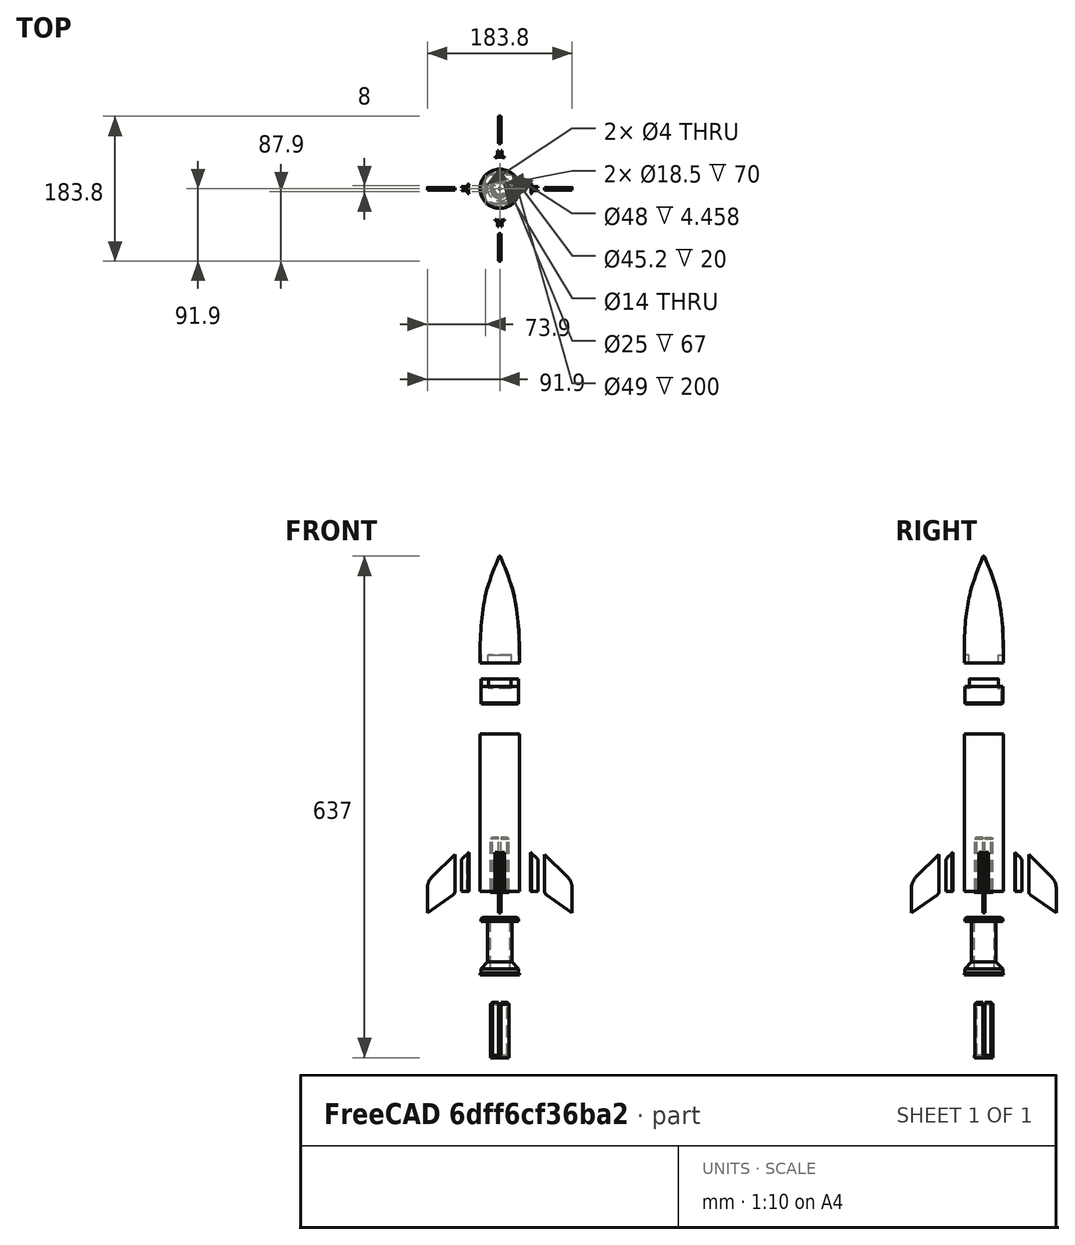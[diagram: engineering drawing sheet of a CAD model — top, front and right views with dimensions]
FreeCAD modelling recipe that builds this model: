
FCSTD DOCUMENT  (FreeCAD 0.19R)
Label: LaMule_V1_eclate
License: All rights reserved
LicenseURL: http://en.wikipedia.org/wiki/All_rights_reserved
objects: Sketcher::SketchObject×26, PartDesign::Pad×16, PartDesign::Body×14, PartDesign::Fillet×12, PartDesign::Pocket×8, PartDesign::Chamfer×7, Mesh::Feature×3, TechDraw::DrawViewSection×3, PartDesign::Revolution×2, App::LinkGroup×2, TechDraw::DrawViewDimension×2, PartDesign::Thickness×1, TechDraw::DrawSVGTemplate×1, TechDraw::DrawViewPart×1, TechDraw::DrawPage×1
note: 132 computed .brp shape members not serialized (recipe doc carries the construction recipe); baked Part::Feature solids carry a one-line shape summary decoded from their .brp

FEATURE [Sketcher::SketchObject] Sketch
  FullyConstrained = true
  MapMode = 5
  Placement = pos=(0,0,0) rot=(1,0,0;1.5708rad)
  Support = -> [XZ_Plane]
  sketch-geometry (12):
    g0: LineSegment StartX=24 StartY=0 StartZ=0 EndX=7 EndY=0 EndZ=0
    g1: LineSegment StartX=7 StartY=0 StartZ=0 EndX=7 EndY=3 EndZ=0
    g2: LineSegment StartX=7 StartY=3 StartZ=0 EndX=12.5 EndY=3 EndZ=0
    g3: LineSegment StartX=12.5 StartY=3 StartZ=0 EndX=12.5 EndY=73 EndZ=0
    g4: LineSegment StartX=12.5 StartY=73 StartZ=0 EndX=25 EndY=73 EndZ=0
    g5: LineSegment StartX=25 StartY=73 StartZ=0 EndX=25 EndY=71 EndZ=0
    g6: LineSegment StartX=25 StartY=71 StartZ=0 EndX=24 EndY=70 EndZ=0
    g7: LineSegment StartX=24 StartY=70 StartZ=0 EndX=24 EndY=65 EndZ=0
    g8: LineSegment StartX=24 StartY=65 StartZ=0 EndX=15.5 EndY=56.5 EndZ=0
    g9: LineSegment StartX=15.5 StartY=56.5 StartZ=0 EndX=15.5 EndY=5 EndZ=0
    g10: LineSegment StartX=15.5 StartY=5 StartZ=0 EndX=24 EndY=5 EndZ=0
    g11: LineSegment StartX=24 StartY=5 StartZ=0 EndX=24 EndY=0 EndZ=0
  constraints (36):
    c: PointOnObject(g0,g-1)
    c: PointOnObject(g0,g-1)
    c: Coincident(g0,g1)
    c: Vertical(g1)
    c: Coincident(g1,g2)
    c: Horizontal(g2)
    c: Coincident(g2,g3)
    c: Vertical(g3)
    c: Coincident(g3,g4)
    c: Horizontal(g4)
    c: Coincident(g4,g5)
    c: Coincident(g5,g6)
    c: Coincident(g6,g7)
    c: Vertical(g7)
    c: Coincident(g7,g8)
    c: Coincident(g8,g9)
    c: Vertical(g9)
    c: Coincident(g9,g10)
    c: Horizontal(g10)
    c: Coincident(g10,g11)
    c: Coincident(g11,g0)
    c: DistanceX(g-2,g2) = 12.5
    c: DistanceY(g3,g3) = 70
    c: DistanceY(g1,g1) = 3
    c: DistanceX(g-2,g4) = 25
    c: Vertical(g5)
    c: DistanceY(g5,g5) = 2
    c: DistanceY(g7,g7) = 5
    c: DistanceX(g-1,g0) = 24
    c: DistanceX(g-2,g7) = 24
    c: Distance(g9,g3) = 3
    c: DistanceY(g11,g11) = 5
    c: Angle(g9,g8) = 2.35619
    c: Angle(g7,g6) = 2.35619
    c: Vertical(g11)
    c: DistanceX(g-2,g0) = 7
FEATURE [PartDesign::Revolution] Revolution
  Angle = 360
  Axis = (0,2e-16,1)
  Base = (0,0,0)
  Placement = pos=(0,0,0) rot=(1,0,0;1.5708rad)
  Profile = -> Sketch
  ReferenceAxis = -> Sketch [V_Axis]
  Reversed = true
FEATURE [PartDesign::Chamfer] Chamfer
  Angle = 45
  Base = -> Revolution [Edge6]
  BaseFeature = -> Revolution
  ChamferType = 0
  FlipDirection = false
  Placement = pos=(0,0,0) rot=(1,0,0;1.5708rad)
  Size = 3
  Size2 = 1
  SupportTransform = false
FEATURE [PartDesign::Chamfer] Chamfer001
  Angle = 45
  Base = -> Chamfer [Edge12]
  BaseFeature = -> Chamfer
  ChamferType = 0
  FlipDirection = false
  Placement = pos=(0,0,0) rot=(1,0,0;1.5708rad)
  Size = 2
  Size2 = 1
  SupportTransform = false
FEATURE [PartDesign::Body] Body  label="support_moteur_V1"
  Group = -> [Sketch,Revolution,Chamfer,Chamfer001]
  Origin = -> Origin
  Placement = pos=(7e-15,0,-33) rot=(0,1,0;3.14159rad)
  Tip = -> Chamfer001
FEATURE [Sketcher::SketchObject] Sketch001
  FullyConstrained = true
  MapMode = 5
  Support = -> [XY_Plane001]
  sketch-geometry (2):
    g0: Circle CenterX=0 CenterY=0 CenterZ=0 NormalX=0 NormalY=0 NormalZ=1 AngleXU=0 Radius=24.5
    g1: Circle CenterX=0 CenterY=0 CenterZ=0 NormalX=0 NormalY=0 NormalZ=1 AngleXU=0 Radius=25
  constraints (4):
    c: Radius(g0) = 24.5
    c: Radius(g1) = 25
    c: Coincident(g0,g-1)
    c: Coincident(g1,g0)
FEATURE [PartDesign::Pad] Pad
  Direction = (1,1,1)
  Length = 200
  Length2 = 100
  Profile = -> Sketch001
  Type = 0
FEATURE [PartDesign::Body] Body001  label="tube_V1"
  Group = -> [Sketch001,Pad]
  Origin = -> Origin001
  Tip = -> Pad
FEATURE [Sketcher::SketchObject] Sketch002
  FullyConstrained = true
  MapMode = 5
  Support = -> [XY_Plane002]
  sketch-geometry (12):
    g0: ArcOfCircle CenterX=0 CenterY=0 CenterZ=0 NormalX=0 NormalY=0 NormalZ=1 AngleXU=0 Radius=25 StartAngle=6.04082 EndAngle=6.52555
    g1: LineSegment StartX=24.2693 StartY=-6 StartZ=0 EndX=25.2982 EndY=-6 EndZ=0
    g2: LineSegment StartX=24.2693 StartY=6 StartZ=0 EndX=25.2982 EndY=6 EndZ=0
    g3: LineSegment StartX=25.8697 StartY=2.6 StartZ=0 EndX=33.4517 EndY=2.6 EndZ=0
    g4: LineSegment StartX=33.4517 StartY=2.6 StartZ=0 EndX=33.4517 EndY=1.6 EndZ=0
    g5: LineSegment StartX=33.4517 StartY=1.6 StartZ=0 EndX=26.4517 EndY=1.6 EndZ=0
    g6: LineSegment StartX=26.4517 StartY=1.6 StartZ=0 EndX=26.4517 EndY=-1.6 EndZ=0
    g7: LineSegment StartX=26.4517 StartY=-1.6 StartZ=0 EndX=33.4517 EndY=-1.6 EndZ=0
    g8: LineSegment StartX=33.4517 StartY=-1.6 StartZ=0 EndX=33.4517 EndY=-2.6 EndZ=0
    g9: LineSegment StartX=33.4517 StartY=-2.6 StartZ=0 EndX=25.8697 EndY=-2.6 EndZ=0
    g10: ArcOfCircle CenterX=0 CenterY=0 CenterZ=0 NormalX=0 NormalY=0 NormalZ=1 AngleXU=0 Radius=26 StartAngle=6.05032 EndAngle=6.18302
    g11: ArcOfCircle CenterX=0 CenterY=0 CenterZ=0 NormalX=0 NormalY=0 NormalZ=1 AngleXU=0 Radius=26 StartAngle=0.100167 EndAngle=0.232868
  constraints (33):
    c: Coincident(g0,g-1)
    c: Radius(g0) = 25
    c: Coincident(g0,g1)
    c: Coincident(g0,g2)
    c: Horizontal(g3)
    c: Coincident(g3,g4)
    c: Coincident(g4,g5)
    c: Horizontal(g5)
    c: Coincident(g5,g6)
    c: Coincident(g6,g7)
    c: Horizontal(g7)
    c: Coincident(g7,g8)
    c: Coincident(g8,g9)
    c: Horizontal(g9)
    c: Coincident(g10,g0)
    c: Coincident(g10,g1)
    c: Coincident(g10,g9)
    c: Coincident(g11,g0)
    c: Coincident(g11,g2)
    c: Coincident(g11,g3)
    c: Radius(g11) = 26
    c: Horizontal(g2)
    c: Horizontal(g1)
    c: Symmetric(g7,g4,g-1)
    c: Vertical(g8)
    c: Vertical(g6)
    c: Distance(g6,g5) = 3.2
    c: DistanceY(g4,g4) = 1
    c: Distance(g5,g0) = 26.5
    c: Symmetric(g3,g8,g-1)
    c: DistanceX(g5,g5) = 7
    c: Symmetric(g2,g1,g-1)
    c: DistanceY(g-1,g2) = 6
FEATURE [PartDesign::Pad] Pad001
  Direction = (1,1,1)
  Length = 50
  Length2 = 100
  Profile = -> Sketch002
  Type = 0
FEATURE [PartDesign::Fillet] Fillet
  Base = -> Pad001 [Edge20,Edge1]
  BaseFeature = -> Pad001
  Radius = 4
  SupportTransform = false
FEATURE [Sketcher::SketchObject] Sketch003
  ExternalGeometry = -> [Fillet]
  FullyConstrained = true
  MapMode = 5
  Placement = pos=(0,-2.6,0) rot=(1,0,0;1.5708rad)
  Support = -> [Fillet]
  sketch-geometry (3):
    g0: LineSegment StartX=33.4517 StartY=50 StartZ=0 EndX=33.4517 EndY=40.8177 EndZ=0
    g1: LineSegment StartX=33.4517 StartY=40.8177 StartZ=0 EndX=24.2693 EndY=50 EndZ=0
    g2: LineSegment StartX=24.2693 StartY=50 StartZ=0 EndX=33.4517 EndY=50 EndZ=0
  constraints (8):
    c: Coincident(g-4,g0)
    c: PointOnObject(g0,g-4)
    c: Coincident(g0,g1)
    c: PointOnObject(g1,g-3)
    c: Coincident(g1,g2)
    c: Coincident(g2,g0)
    c: Horizontal(g2)
    c: Angle(g1,g2) = 0.785398
FEATURE [PartDesign::Pocket] Pocket
  BaseFeature = -> Fillet
  Length = 23
  Length2 = 100
  Midplane = true
  Profile = -> Sketch003
  Type = 1
FEATURE [PartDesign::Body] Body002  label="support_aileron_V1"
  Group = -> [Sketch002,Pad001,Fillet,Sketch003,Pocket]
  Origin = -> Origin002
  Placement = pos=(15,0,0) rot=(0,0,1;0rad)
  Tip = -> Pocket
FEATURE [Sketcher::SketchObject] Sketch004
  FullyConstrained = true
  MapMode = 5
  Support = -> [XY_Plane003]
  sketch-geometry (12):
    g0: ArcOfCircle CenterX=0 CenterY=0 CenterZ=0 NormalX=0 NormalY=0 NormalZ=1 AngleXU=0 Radius=25 StartAngle=6.04082 EndAngle=6.52555
    g1: LineSegment StartX=24.2693 StartY=-6 StartZ=0 EndX=25.2982 EndY=-6 EndZ=0
    g2: LineSegment StartX=24.2693 StartY=6 StartZ=0 EndX=25.2982 EndY=6 EndZ=0
    g3: LineSegment StartX=25.8697 StartY=2.6 StartZ=0 EndX=33.4517 EndY=2.6 EndZ=0
    g4: LineSegment StartX=33.4517 StartY=2.6 StartZ=0 EndX=33.4517 EndY=1.6 EndZ=0
    g5: LineSegment StartX=33.4517 StartY=1.6 StartZ=0 EndX=26.4517 EndY=1.6 EndZ=0
    g6: LineSegment StartX=26.4517 StartY=1.6 StartZ=0 EndX=26.4517 EndY=-1.6 EndZ=0
    g7: LineSegment StartX=26.4517 StartY=-1.6 StartZ=0 EndX=33.4517 EndY=-1.6 EndZ=0
    g8: LineSegment StartX=33.4517 StartY=-1.6 StartZ=0 EndX=33.4517 EndY=-2.6 EndZ=0
    g9: LineSegment StartX=33.4517 StartY=-2.6 StartZ=0 EndX=25.8697 EndY=-2.6 EndZ=0
    g10: ArcOfCircle CenterX=0 CenterY=0 CenterZ=0 NormalX=0 NormalY=0 NormalZ=1 AngleXU=0 Radius=26 StartAngle=6.05032 EndAngle=6.18302
    g11: ArcOfCircle CenterX=0 CenterY=0 CenterZ=0 NormalX=0 NormalY=0 NormalZ=1 AngleXU=0 Radius=26 StartAngle=0.100167 EndAngle=0.232868
  constraints (33):
    c: Coincident(g0,g-1)
    c: Radius(g0) = 25
    c: Coincident(g0,g1)
    c: Coincident(g0,g2)
    c: Horizontal(g3)
    c: Coincident(g3,g4)
    c: Coincident(g4,g5)
    c: Horizontal(g5)
    c: Coincident(g5,g6)
    c: Coincident(g6,g7)
    c: Horizontal(g7)
    c: Coincident(g7,g8)
    c: Coincident(g8,g9)
    c: Horizontal(g9)
    c: Coincident(g10,g0)
    c: Coincident(g10,g1)
    c: Coincident(g10,g9)
    c: Coincident(g11,g0)
    c: Coincident(g11,g2)
    c: Coincident(g11,g3)
    c: Radius(g11) = 26
    c: Horizontal(g2)
    c: Horizontal(g1)
    c: Symmetric(g7,g4,g-1)
    c: Vertical(g8)
    c: Vertical(g6)
    c: Distance(g6,g5) = 3.2
    c: DistanceY(g4,g4) = 1
    c: Distance(g5,g0) = 26.5
    c: Symmetric(g3,g8,g-1)
    c: DistanceX(g5,g5) = 7
    c: Symmetric(g2,g1,g-1)
    c: DistanceY(g-1,g2) = 6
FEATURE [PartDesign::Pad] Pad002
  Direction = (1,1,1)
  Length = 50
  Length2 = 100
  Profile = -> Sketch004
  Type = 0
FEATURE [PartDesign::Fillet] Fillet001
  Base = -> Pad002 [Edge20,Edge1]
  BaseFeature = -> Pad002
  Radius = 4
  SupportTransform = false
FEATURE [Sketcher::SketchObject] Sketch005
  ExternalGeometry = -> [Fillet001]
  FullyConstrained = true
  MapMode = 5
  Placement = pos=(0,-2.6,0) rot=(1,0,0;1.5708rad)
  Support = -> [Fillet001]
  sketch-geometry (3):
    g0: LineSegment StartX=33.4517 StartY=50 StartZ=0 EndX=33.4517 EndY=40.8177 EndZ=0
    g1: LineSegment StartX=33.4517 StartY=40.8177 StartZ=0 EndX=24.2693 EndY=50 EndZ=0
    g2: LineSegment StartX=24.2693 StartY=50 StartZ=0 EndX=33.4517 EndY=50 EndZ=0
  constraints (8):
    c: Coincident(g-4,g0)
    c: PointOnObject(g0,g-4)
    c: Coincident(g0,g1)
    c: PointOnObject(g1,g-3)
    c: Coincident(g1,g2)
    c: Coincident(g2,g0)
    c: Horizontal(g2)
    c: Angle(g1,g2) = 0.785398
FEATURE [PartDesign::Pocket] Pocket001
  BaseFeature = -> Fillet001
  Length = 23
  Length2 = 100
  Midplane = true
  Profile = -> Sketch005
  Type = 1
FEATURE [PartDesign::Body] Body003  label="support_aileron_V002"
  Group = -> [Sketch004,Pad002,Fillet001,Sketch005,Pocket001]
  Origin = -> Origin003
  Placement = pos=(3.3e-15,15,0) rot=(0,0,1;1.5708rad)
  Tip = -> Pocket001
FEATURE [Sketcher::SketchObject] Sketch006
  FullyConstrained = true
  MapMode = 5
  Support = -> [XY_Plane004]
  sketch-geometry (12):
    g0: ArcOfCircle CenterX=0 CenterY=0 CenterZ=0 NormalX=0 NormalY=0 NormalZ=1 AngleXU=0 Radius=25 StartAngle=6.04082 EndAngle=6.52555
    g1: LineSegment StartX=24.2693 StartY=-6 StartZ=0 EndX=25.2982 EndY=-6 EndZ=0
    g2: LineSegment StartX=24.2693 StartY=6 StartZ=0 EndX=25.2982 EndY=6 EndZ=0
    g3: LineSegment StartX=25.8697 StartY=2.6 StartZ=0 EndX=33.4517 EndY=2.6 EndZ=0
    g4: LineSegment StartX=33.4517 StartY=2.6 StartZ=0 EndX=33.4517 EndY=1.6 EndZ=0
    g5: LineSegment StartX=33.4517 StartY=1.6 StartZ=0 EndX=26.4517 EndY=1.6 EndZ=0
    g6: LineSegment StartX=26.4517 StartY=1.6 StartZ=0 EndX=26.4517 EndY=-1.6 EndZ=0
    g7: LineSegment StartX=26.4517 StartY=-1.6 StartZ=0 EndX=33.4517 EndY=-1.6 EndZ=0
    g8: LineSegment StartX=33.4517 StartY=-1.6 StartZ=0 EndX=33.4517 EndY=-2.6 EndZ=0
    g9: LineSegment StartX=33.4517 StartY=-2.6 StartZ=0 EndX=25.8697 EndY=-2.6 EndZ=0
    g10: ArcOfCircle CenterX=0 CenterY=0 CenterZ=0 NormalX=0 NormalY=0 NormalZ=1 AngleXU=0 Radius=26 StartAngle=6.05032 EndAngle=6.18302
    g11: ArcOfCircle CenterX=0 CenterY=0 CenterZ=0 NormalX=0 NormalY=0 NormalZ=1 AngleXU=0 Radius=26 StartAngle=0.100167 EndAngle=0.232868
  constraints (33):
    c: Coincident(g0,g-1)
    c: Radius(g0) = 25
    c: Coincident(g0,g1)
    c: Coincident(g0,g2)
    c: Horizontal(g3)
    c: Coincident(g3,g4)
    c: Coincident(g4,g5)
    c: Horizontal(g5)
    c: Coincident(g5,g6)
    c: Coincident(g6,g7)
    c: Horizontal(g7)
    c: Coincident(g7,g8)
    c: Coincident(g8,g9)
    c: Horizontal(g9)
    c: Coincident(g10,g0)
    c: Coincident(g10,g1)
    c: Coincident(g10,g9)
    c: Coincident(g11,g0)
    c: Coincident(g11,g2)
    c: Coincident(g11,g3)
    c: Radius(g11) = 26
    c: Horizontal(g2)
    c: Horizontal(g1)
    c: Symmetric(g7,g4,g-1)
    c: Vertical(g8)
    c: Vertical(g6)
    c: Distance(g6,g5) = 3.2
    c: DistanceY(g4,g4) = 1
    c: Distance(g5,g0) = 26.5
    c: Symmetric(g3,g8,g-1)
    c: DistanceX(g5,g5) = 7
    c: Symmetric(g2,g1,g-1)
    c: DistanceY(g-1,g2) = 6
FEATURE [PartDesign::Pad] Pad003
  Direction = (1,1,1)
  Length = 50
  Length2 = 100
  Profile = -> Sketch006
  Type = 0
FEATURE [PartDesign::Fillet] Fillet002
  Base = -> Pad003 [Edge20,Edge1]
  BaseFeature = -> Pad003
  Radius = 4
  SupportTransform = false
FEATURE [Sketcher::SketchObject] Sketch007
  ExternalGeometry = -> [Fillet002]
  FullyConstrained = true
  MapMode = 5
  Placement = pos=(0,-2.6,0) rot=(1,0,0;1.5708rad)
  Support = -> [Fillet002]
  sketch-geometry (3):
    g0: LineSegment StartX=33.4517 StartY=50 StartZ=0 EndX=33.4517 EndY=40.8177 EndZ=0
    g1: LineSegment StartX=33.4517 StartY=40.8177 StartZ=0 EndX=24.2693 EndY=50 EndZ=0
    g2: LineSegment StartX=24.2693 StartY=50 StartZ=0 EndX=33.4517 EndY=50 EndZ=0
  constraints (8):
    c: Coincident(g-4,g0)
    c: PointOnObject(g0,g-4)
    c: Coincident(g0,g1)
    c: PointOnObject(g1,g-3)
    c: Coincident(g1,g2)
    c: Coincident(g2,g0)
    c: Horizontal(g2)
    c: Angle(g1,g2) = 0.785398
FEATURE [PartDesign::Pocket] Pocket002
  BaseFeature = -> Fillet002
  Length = 23
  Length2 = 100
  Midplane = true
  Profile = -> Sketch007
  Type = 1
FEATURE [PartDesign::Body] Body004  label="support_aileron_V003"
  Group = -> [Sketch006,Pad003,Fillet002,Sketch007,Pocket002]
  Origin = -> Origin004
  Placement = pos=(-15,0,0) rot=(0,0,1;3.14159rad)
  Tip = -> Pocket002
FEATURE [Sketcher::SketchObject] Sketch008
  FullyConstrained = true
  MapMode = 5
  Support = -> [XY_Plane005]
  sketch-geometry (12):
    g0: ArcOfCircle CenterX=0 CenterY=0 CenterZ=0 NormalX=0 NormalY=0 NormalZ=1 AngleXU=0 Radius=25 StartAngle=6.04082 EndAngle=6.52555
    g1: LineSegment StartX=24.2693 StartY=-6 StartZ=0 EndX=25.2982 EndY=-6 EndZ=0
    g2: LineSegment StartX=24.2693 StartY=6 StartZ=0 EndX=25.2982 EndY=6 EndZ=0
    g3: LineSegment StartX=25.8697 StartY=2.6 StartZ=0 EndX=33.4517 EndY=2.6 EndZ=0
    g4: LineSegment StartX=33.4517 StartY=2.6 StartZ=0 EndX=33.4517 EndY=1.6 EndZ=0
    g5: LineSegment StartX=33.4517 StartY=1.6 StartZ=0 EndX=26.4517 EndY=1.6 EndZ=0
    g6: LineSegment StartX=26.4517 StartY=1.6 StartZ=0 EndX=26.4517 EndY=-1.6 EndZ=0
    g7: LineSegment StartX=26.4517 StartY=-1.6 StartZ=0 EndX=33.4517 EndY=-1.6 EndZ=0
    g8: LineSegment StartX=33.4517 StartY=-1.6 StartZ=0 EndX=33.4517 EndY=-2.6 EndZ=0
    g9: LineSegment StartX=33.4517 StartY=-2.6 StartZ=0 EndX=25.8697 EndY=-2.6 EndZ=0
    g10: ArcOfCircle CenterX=0 CenterY=0 CenterZ=0 NormalX=0 NormalY=0 NormalZ=1 AngleXU=0 Radius=26 StartAngle=6.05032 EndAngle=6.18302
    g11: ArcOfCircle CenterX=0 CenterY=0 CenterZ=0 NormalX=0 NormalY=0 NormalZ=1 AngleXU=0 Radius=26 StartAngle=0.100167 EndAngle=0.232868
  constraints (33):
    c: Coincident(g0,g-1)
    c: Radius(g0) = 25
    c: Coincident(g0,g1)
    c: Coincident(g0,g2)
    c: Horizontal(g3)
    c: Coincident(g3,g4)
    c: Coincident(g4,g5)
    c: Horizontal(g5)
    c: Coincident(g5,g6)
    c: Coincident(g6,g7)
    c: Horizontal(g7)
    c: Coincident(g7,g8)
    c: Coincident(g8,g9)
    c: Horizontal(g9)
    c: Coincident(g10,g0)
    c: Coincident(g10,g1)
    c: Coincident(g10,g9)
    c: Coincident(g11,g0)
    c: Coincident(g11,g2)
    c: Coincident(g11,g3)
    c: Radius(g11) = 26
    c: Horizontal(g2)
    c: Horizontal(g1)
    c: Symmetric(g7,g4,g-1)
    c: Vertical(g8)
    c: Vertical(g6)
    c: Distance(g6,g5) = 3.2
    c: DistanceY(g4,g4) = 1
    c: Distance(g5,g0) = 26.5
    c: Symmetric(g3,g8,g-1)
    c: DistanceX(g5,g5) = 7
    c: Symmetric(g2,g1,g-1)
    c: DistanceY(g-1,g2) = 6
FEATURE [PartDesign::Pad] Pad004
  Direction = (1,1,1)
  Length = 50
  Length2 = 100
  Profile = -> Sketch008
  Type = 0
FEATURE [PartDesign::Fillet] Fillet003
  Base = -> Pad004 [Edge20,Edge1]
  BaseFeature = -> Pad004
  Radius = 4
  SupportTransform = false
FEATURE [Sketcher::SketchObject] Sketch009
  ExternalGeometry = -> [Fillet003]
  FullyConstrained = true
  MapMode = 5
  Placement = pos=(0,-2.6,0) rot=(1,0,0;1.5708rad)
  Support = -> [Fillet003]
  sketch-geometry (3):
    g0: LineSegment StartX=33.4517 StartY=50 StartZ=0 EndX=33.4517 EndY=40.8177 EndZ=0
    g1: LineSegment StartX=33.4517 StartY=40.8177 StartZ=0 EndX=24.2693 EndY=50 EndZ=0
    g2: LineSegment StartX=24.2693 StartY=50 StartZ=0 EndX=33.4517 EndY=50 EndZ=0
  constraints (8):
    c: Coincident(g-4,g0)
    c: PointOnObject(g0,g-4)
    c: Coincident(g0,g1)
    c: PointOnObject(g1,g-3)
    c: Coincident(g1,g2)
    c: Coincident(g2,g0)
    c: Horizontal(g2)
    c: Angle(g1,g2) = 0.785398
FEATURE [PartDesign::Pocket] Pocket003
  BaseFeature = -> Fillet003
  Length = 23
  Length2 = 100
  Midplane = true
  Profile = -> Sketch009
  Type = 1
FEATURE [PartDesign::Body] Body005  label="support_aileron_V004"
  Group = -> [Sketch008,Pad004,Fillet003,Sketch009,Pocket003]
  Origin = -> Origin005
  Placement = pos=(3.3e-15,-15,0) rot=(0,0,-1;1.5708rad)
  Tip = -> Pocket003
FEATURE [App::LinkGroup] LinkGroup  label="support_ailerons_V1"
  ElementList = -> [Body005,Body004,Body003,Body002]
  LinkMode = 0
FEATURE [Sketcher::SketchObject] Sketch010
  FullyConstrained = true
  MapMode = 5
  Placement = pos=(0,0,0) rot=(0.57735,0.57735,0.57735;2.0944rad)
  Support = -> [YZ_Plane006]
  sketch-geometry (4):
    g0: LineSegment StartX=27 StartY=-2.5 StartZ=0 EndX=61.9 EndY=-27.4 EndZ=0
    g1: LineSegment StartX=61.9 StartY=-27.4 StartZ=0 EndX=61.9 EndY=12.6 EndZ=0
    g2: LineSegment StartX=61.9 StartY=12.6 StartZ=0 EndX=27 EndY=47.5 EndZ=0
    g3: LineSegment StartX=27 StartY=47.5 StartZ=0 EndX=27 EndY=-2.5 EndZ=0
  constraints (12):
    c: Coincident(g0,g1)
    c: Vertical(g1)
    c: Coincident(g1,g2)
    c: Coincident(g2,g3)
    c: Coincident(g3,g0)
    c: Vertical(g3)
    c: DistanceY(g3,g3) = 50
    c: DistanceY(g-1,g2) = 47.5
    c: DistanceX(g-2,g0) = 27
    c: Angle(g3,g2) = 0.785398
    c: DistanceY(g1,g1) = 40
    c: DistanceX(g-2,g0) = 61.9
FEATURE [PartDesign::Pad] Pad005
  Direction = (1,1,1)
  Length = 3
  Length2 = 100
  Midplane = true
  Placement = pos=(0,0,0) rot=(0.57735,0.57735,0.57735;2.0944rad)
  Profile = -> Sketch010
  Type = 0
FEATURE [PartDesign::Fillet] Fillet004
  Base = -> Pad005 [Edge5]
  BaseFeature = -> Pad005
  Placement = pos=(0,0,0) rot=(0.57735,0.57735,0.57735;2.0944rad)
  Radius = 20
  SupportTransform = false
FEATURE [PartDesign::Fillet] Fillet005
  Base = -> Fillet004 [Edge11]
  BaseFeature = -> Fillet004
  Placement = pos=(0,0,0) rot=(0.57735,0.57735,0.57735;2.0944rad)
  Radius = 5
  SupportTransform = false
FEATURE [PartDesign::Body] Body006  label="ailerons_V1"
  Group = -> [Sketch010,Pad005,Fillet004,Fillet005]
  Origin = -> Origin006
  Placement = pos=(0,30,0) rot=(0,0,1;0rad)
  Tip = -> Fillet005
FEATURE [Sketcher::SketchObject] Sketch011
  FullyConstrained = true
  MapMode = 5
  Placement = pos=(0,0,0) rot=(0.57735,0.57735,0.57735;2.0944rad)
  Support = -> [YZ_Plane007]
  sketch-geometry (4):
    g0: LineSegment StartX=27 StartY=-2.5 StartZ=0 EndX=61.9 EndY=-27.4 EndZ=0
    g1: LineSegment StartX=61.9 StartY=-27.4 StartZ=0 EndX=61.9 EndY=12.6 EndZ=0
    g2: LineSegment StartX=61.9 StartY=12.6 StartZ=0 EndX=27 EndY=47.5 EndZ=0
    g3: LineSegment StartX=27 StartY=47.5 StartZ=0 EndX=27 EndY=-2.5 EndZ=0
  constraints (12):
    c: Coincident(g0,g1)
    c: Vertical(g1)
    c: Coincident(g1,g2)
    c: Coincident(g2,g3)
    c: Coincident(g3,g0)
    c: Vertical(g3)
    c: DistanceY(g3,g3) = 50
    c: DistanceY(g-1,g2) = 47.5
    c: DistanceX(g-2,g0) = 27
    c: Angle(g3,g2) = 0.785398
    c: DistanceY(g1,g1) = 40
    c: DistanceX(g-2,g0) = 61.9
FEATURE [PartDesign::Pad] Pad006
  Direction = (1,1,1)
  Length = 3
  Length2 = 100
  Midplane = true
  Placement = pos=(0,0,0) rot=(0.57735,0.57735,0.57735;2.0944rad)
  Profile = -> Sketch011
  Type = 0
FEATURE [PartDesign::Fillet] Fillet006
  Base = -> Pad006 [Edge5]
  BaseFeature = -> Pad006
  Placement = pos=(0,0,0) rot=(0.57735,0.57735,0.57735;2.0944rad)
  Radius = 20
  SupportTransform = false
FEATURE [PartDesign::Fillet] Fillet007
  Base = -> Fillet006 [Edge11]
  BaseFeature = -> Fillet006
  Placement = pos=(0,0,0) rot=(0.57735,0.57735,0.57735;2.0944rad)
  Radius = 5
  SupportTransform = false
FEATURE [PartDesign::Body] Body007  label="ailerons_V002"
  Group = -> [Sketch011,Pad006,Fillet006,Fillet007]
  Origin = -> Origin007
  Placement = pos=(0,-30,0) rot=(0,0,1;3.14159rad)
  Tip = -> Fillet007
FEATURE [Sketcher::SketchObject] Sketch012
  FullyConstrained = true
  MapMode = 5
  Placement = pos=(0,0,0) rot=(0.57735,0.57735,0.57735;2.0944rad)
  Support = -> [YZ_Plane008]
  sketch-geometry (4):
    g0: LineSegment StartX=27 StartY=-2.5 StartZ=0 EndX=61.9 EndY=-27.4 EndZ=0
    g1: LineSegment StartX=61.9 StartY=-27.4 StartZ=0 EndX=61.9 EndY=12.6 EndZ=0
    g2: LineSegment StartX=61.9 StartY=12.6 StartZ=0 EndX=27 EndY=47.5 EndZ=0
    g3: LineSegment StartX=27 StartY=47.5 StartZ=0 EndX=27 EndY=-2.5 EndZ=0
  constraints (12):
    c: Coincident(g0,g1)
    c: Vertical(g1)
    c: Coincident(g1,g2)
    c: Coincident(g2,g3)
    c: Coincident(g3,g0)
    c: Vertical(g3)
    c: DistanceY(g3,g3) = 50
    c: DistanceY(g-1,g2) = 47.5
    c: DistanceX(g-2,g0) = 27
    c: Angle(g3,g2) = 0.785398
    c: DistanceY(g1,g1) = 40
    c: DistanceX(g-2,g0) = 61.9
FEATURE [PartDesign::Pad] Pad007
  Direction = (1,1,1)
  Length = 3
  Length2 = 100
  Midplane = true
  Placement = pos=(0,0,0) rot=(0.57735,0.57735,0.57735;2.0944rad)
  Profile = -> Sketch012
  Type = 0
FEATURE [PartDesign::Fillet] Fillet008
  Base = -> Pad007 [Edge5]
  BaseFeature = -> Pad007
  Placement = pos=(0,0,0) rot=(0.57735,0.57735,0.57735;2.0944rad)
  Radius = 20
  SupportTransform = false
FEATURE [PartDesign::Fillet] Fillet009
  Base = -> Fillet008 [Edge11]
  BaseFeature = -> Fillet008
  Placement = pos=(0,0,0) rot=(0.57735,0.57735,0.57735;2.0944rad)
  Radius = 5
  SupportTransform = false
FEATURE [PartDesign::Body] Body008  label="ailerons_V003"
  Group = -> [Sketch012,Pad007,Fillet008,Fillet009]
  Origin = -> Origin008
  Placement = pos=(-30,6.7e-15,0) rot=(0,0,1;1.5708rad)
  Tip = -> Fillet009
FEATURE [Sketcher::SketchObject] Sketch013
  FullyConstrained = true
  MapMode = 5
  Placement = pos=(0,0,0) rot=(0.57735,0.57735,0.57735;2.0944rad)
  Support = -> [YZ_Plane009]
  sketch-geometry (4):
    g0: LineSegment StartX=27 StartY=-2.5 StartZ=0 EndX=61.9 EndY=-27.4 EndZ=0
    g1: LineSegment StartX=61.9 StartY=-27.4 StartZ=0 EndX=61.9 EndY=12.6 EndZ=0
    g2: LineSegment StartX=61.9 StartY=12.6 StartZ=0 EndX=27 EndY=47.5 EndZ=0
    g3: LineSegment StartX=27 StartY=47.5 StartZ=0 EndX=27 EndY=-2.5 EndZ=0
  constraints (12):
    c: Coincident(g0,g1)
    c: Vertical(g1)
    c: Coincident(g1,g2)
    c: Coincident(g2,g3)
    c: Coincident(g3,g0)
    c: Vertical(g3)
    c: DistanceY(g3,g3) = 50
    c: DistanceY(g-1,g2) = 47.5
    c: DistanceX(g-2,g0) = 27
    c: Angle(g3,g2) = 0.785398
    c: DistanceY(g1,g1) = 40
    c: DistanceX(g-2,g0) = 61.9
FEATURE [PartDesign::Pad] Pad008
  Direction = (1,1,1)
  Length = 3
  Length2 = 100
  Midplane = true
  Placement = pos=(0,0,0) rot=(0.57735,0.57735,0.57735;2.0944rad)
  Profile = -> Sketch013
  Type = 0
FEATURE [PartDesign::Fillet] Fillet010
  Base = -> Pad008 [Edge5]
  BaseFeature = -> Pad008
  Placement = pos=(0,0,0) rot=(0.57735,0.57735,0.57735;2.0944rad)
  Radius = 20
  SupportTransform = false
FEATURE [PartDesign::Fillet] Fillet011
  Base = -> Fillet010 [Edge11]
  BaseFeature = -> Fillet010
  Placement = pos=(0,0,0) rot=(0.57735,0.57735,0.57735;2.0944rad)
  Radius = 5
  SupportTransform = false
FEATURE [PartDesign::Body] Body009  label="ailerons_V004"
  Group = -> [Sketch013,Pad008,Fillet010,Fillet011]
  Origin = -> Origin009
  Placement = pos=(30,6.7e-15,0) rot=(0,0,-1;1.5708rad)
  Tip = -> Fillet011
FEATURE [App::LinkGroup] LinkGroup001  label="ailerons"
  ElementList = -> [Body009,Body008,Body007,Body006]
  LinkMode = 0
FEATURE [Sketcher::SketchObject] Sketch014
  FullyConstrained = true
  MapMode = 5
  Support = -> [XY_Plane010]
  sketch-geometry (12):
    g0: LineSegment StartX=0 StartY=0 StartZ=0 EndX=134.73 EndY=0 EndZ=0
    g1: LineSegment StartX=134.73 StartY=-24 StartZ=0 EndX=134.73 EndY=0 EndZ=0
    g2: LineSegment StartX=134.73 StartY=-24 StartZ=0 EndX=120.272 EndY=-24 EndZ=0
    g3-g7: Circle x5 (B-spline internal-alignment scaffolding for g8; pole/knot coordinates omitted)
    g8: BSplineCurve PolesCount=5 KnotsCount=3 Degree=3 IsPeriodic=0
    g9: GeomPoint X=120.272 Y=-24 Z=0
    g10: GeomPoint X=62.1183 Y=-19.6849 Z=0
    g11: GeomPoint X=0 Y=0 Z=0
  constraints (23):
    c: Coincident(g0,g-1)
    c: PointOnObject(g0,g-1)
    c: Coincident(g1,g0)
    c: Vertical(g1)
    c: Coincident(g2,g1)
    c: Horizontal(g2)
    c: Coincident(g8,g2)
    c: Weight(g3) = 1
    c: Equal(g3, g4-g7) x4
    c: Coincident(g8,g0)
    c: InternalAlignment(g3-g7 -> g8) x5
    c: InternalAlignment(g9,g8)
    c: InternalAlignment(g10,g8)
    c: InternalAlignment(g11,g8)
    c: DistanceX(g6) = 33.4091
    c: DistanceY(g6) = -14.1378
    c: DistanceX(g5) = 61.0359
    c: DistanceY(g5) = -20.426
    c: DistanceX(g4) = 92.9923
    c: DistanceY(g4) = -23.75
    c: DistanceX(g2) = 120.272
    c: DistanceY(g2) = -24
    c: DistanceX(g0,g0) = 134.73
FEATURE [PartDesign::Revolution] Revolution001
  Angle = 360
  Axis = (1,0,0)
  Base = (0,0,0)
  Profile = -> Sketch014
  ReferenceAxis = -> X_Axis010
  Reversed = true
FEATURE [PartDesign::Thickness] Thickness
  Base = -> Revolution001 [Face1]
  BaseFeature = -> Revolution001
  Intersection = false
  Join = 0
  Mode = 0
  SupportTransform = false
  Value = 1
FEATURE [Sketcher::SketchObject] Sketch015
  FullyConstrained = true
  MapMode = 5
  Placement = pos=(134.73,0,0) rot=(0.57735,0.57735,0.57735;2.0944rad)
  Support = -> [Thickness]
  sketch-geometry (5):
    g0: Circle CenterX=1.1e-15 CenterY=0 CenterZ=0 NormalX=0 NormalY=0 NormalZ=1 AngleXU=0 Radius=25
    g1: ArcOfCircle CenterX=1.1e-15 CenterY=0 CenterZ=0 NormalX=0 NormalY=0 NormalZ=1 AngleXU=0 Radius=24 StartAngle=0.675132 EndAngle=2.46646
    g2: ArcOfCircle CenterX=1.1e-15 CenterY=0 CenterZ=0 NormalX=0 NormalY=0 NormalZ=1 AngleXU=0 Radius=24 StartAngle=3.81672 EndAngle=5.60805
    g3: LineSegment StartX=-18.735 StartY=15 StartZ=0 EndX=-18.735 EndY=-15 EndZ=0
    g4: LineSegment StartX=18.735 StartY=15 StartZ=0 EndX=18.735 EndY=-15 EndZ=0
  constraints (14):
    c: Coincident(g0,g-1)
    c: Radius(g0) = 25
    c: Coincident(g1,g0)
    c: Coincident(g2,g0)
    c: Symmetric(g2,g2,g-2)
    c: Symmetric(g2,g1,g-1)
    c: Radius(g1) = 24
    c: Equal(g1,g2)
    c: Coincident(g3,g1)
    c: Coincident(g3,g2)
    c: Coincident(g4,g1)
    c: Coincident(g4,g2)
    c: Symmetric(g1,g1,g-2)
    c: DistanceY(g4,g4) = 30
FEATURE [PartDesign::Pad] Pad009
  BaseFeature = -> Thickness
  Direction = (1,1,1)
  Length = 10
  Length2 = 100
  Profile = -> Sketch015
  Reversed = true
  Type = 0
FEATURE [PartDesign::Chamfer] Chamfer002
  Angle = 45
  Base = -> Pad009 [Edge9,Edge6]
  BaseFeature = -> Pad009
  ChamferType = 0
  FlipDirection = false
  Size = 1
  Size2 = 1
  SupportTransform = false
FEATURE [PartDesign::Body] Body010  label="coiffe_V1"
  Group = -> [Sketch014,Revolution001,Thickness,Sketch015,Pad009,Chamfer002]
  Origin = -> Origin010
  Placement = pos=(-9.4e-14,0,425) rot=(0,1,0;1.5708rad)
  Tip = -> Chamfer002
FEATURE [Mesh::Feature] Mesh  label="coiffe_V1 (Meshed)"
FEATURE [TechDraw::DrawSVGTemplate] Template
  EditableTexts = Approved1=N/A; Approved2=N/A; CheckedBy=Papas Inventeurs; Code=Code; CompanyAddress=planête Terre, système solaire; CompanyName=Lift Off; DrawingNumber=1; DrawingTitle1=LaMule; DrawingTitle2=Envoyons quelque chose en l'air!; DrawingTitle3="Just because"; DrawnBy=Maël & PéPé; Revision=Rev 1; Scale=Scale; Sheet=Page 1 de 1
  Height = 215.9
  Orientation = 1
  Width = 279.4
FEATURE [Sketcher::SketchObject] Sketch016
  FullyConstrained = true
  MapMode = 5
  Support = -> [XY_Plane011]
  sketch-geometry (8):
    g0: ArcOfCircle CenterX=0 CenterY=-2.3e-15 CenterZ=0 NormalX=0 NormalY=0 NormalZ=1 AngleXU=0 Radius=23.8 StartAngle=2.2259 EndAngle=4.05728
    g1: ArcOfCircle CenterX=0 CenterY=-2.3e-15 CenterZ=0 NormalX=0 NormalY=0 NormalZ=1 AngleXU=0 Radius=23.8 StartAngle=5.3675 EndAngle=7.19888
    g2: LineSegment StartX=-14.5 StartY=-18.873 StartZ=0 EndX=14.5 EndY=-18.873 EndZ=0
    g3: LineSegment StartX=-14.5 StartY=18.873 StartZ=0 EndX=14.5 EndY=18.873 EndZ=0
    g4: ArcOfCircle CenterX=0 CenterY=-2.3e-15 CenterZ=0 NormalX=0 NormalY=0 NormalZ=1 AngleXU=0 Radius=22.6 StartAngle=2.22941 EndAngle=4.05377
    g5: ArcOfCircle CenterX=0 CenterY=-2.3e-15 CenterZ=0 NormalX=0 NormalY=0 NormalZ=1 AngleXU=0 Radius=22.6 StartAngle=5.371 EndAngle=7.19537
    g6: LineSegment StartX=-13.8317 StartY=17.873 StartZ=0 EndX=13.8317 EndY=17.873 EndZ=0
    g7: LineSegment StartX=13.8317 StartY=-17.873 StartZ=0 EndX=-13.8317 EndY=-17.873 EndZ=0
  constraints (22):
    c: Coincident(g0,g-1)
    c: Coincident(g0,g1)
    c: Coincident(g0,g2)
    c: Coincident(g1,g2)
    c: Coincident(g1,g3)
    c: Coincident(g0,g3)
    c: Symmetric(g1,g0,g-2)
    c: Symmetric(g0,g1,g-2)
    c: Radius(g1) = 23.8
    c: Symmetric(g0,g0,g-1)
    c: DistanceX(g2,g2) = 29
    c: Coincident(g4,g0)
    c: Coincident(g5,g0)
    c: Coincident(g6,g4)
    c: Coincident(g6,g5)
    c: Coincident(g7,g5)
    c: Coincident(g7,g4)
    c: Symmetric(g5,g5,g-1)
    c: Symmetric(g5,g4,g-2)
    c: Radius(g5) = 22.6
    c: Horizontal(g7)
    c: Distance(g4,g3) = 1
FEATURE [PartDesign::Pad] Pad010
  Direction = (1,1,1)
  Length = 10
  Length2 = 100
  Profile = -> Sketch016
  Type = 0
FEATURE [PartDesign::Chamfer] Chamfer003
  Angle = 45
  Base = -> Pad010 [Edge7,Edge12]
  BaseFeature = -> Pad010
  ChamferType = 0
  FlipDirection = false
  Size = 0.5
  Size2 = 1
  SupportTransform = false
FEATURE [Sketcher::SketchObject] Sketch017
  FullyConstrained = true
  MapMode = 5
  Placement = pos=(0,0,0) rot=(1,0,0;3.14159rad)
  Support = -> [Chamfer003]
  sketch-geometry (2):
    g0: Circle CenterX=0 CenterY=0 CenterZ=0 NormalX=0 NormalY=0 NormalZ=1 AngleXU=0 Radius=23.9
    g1: Circle CenterX=0 CenterY=0 CenterZ=0 NormalX=0 NormalY=0 NormalZ=1 AngleXU=0 Radius=22.6
  constraints (4):
    c: Coincident(g0,g-1)
    c: Radius(g0) = 23.9
    c: Coincident(g1,g0)
    c: Radius(g1) = 22.6
FEATURE [PartDesign::Pad] Pad011
  BaseFeature = -> Chamfer003
  Direction = (1,1,1)
  Length = 20
  Length2 = 100
  Profile = -> Sketch017
  Type = 0
FEATURE [Sketcher::SketchObject] Sketch018
  ExternalGeometry = -> [Pad011]
  FullyConstrained = true
  MapMode = 5
  Placement = pos=(0,0,0) rot=(1,0,0;3.14159rad)
  Support = -> [Pad011]
  sketch-geometry (4):
    g0: ArcOfCircle CenterX=-1.1e-15 CenterY=0 CenterZ=0 NormalX=0 NormalY=0 NormalZ=1 AngleXU=0 Radius=23.9 StartAngle=3.98637 EndAngle=5.43841
    g1: ArcOfCircle CenterX=-1.1e-15 CenterY=0 CenterZ=0 NormalX=0 NormalY=0 NormalZ=1 AngleXU=0 Radius=23.9 StartAngle=0.844779 EndAngle=2.29681
    g2: LineSegment StartX=-15.8671 StartY=17.873 StartZ=0 EndX=15.8671 EndY=17.873 EndZ=0
    g3: LineSegment StartX=-15.8671 StartY=-17.873 StartZ=0 EndX=15.8671 EndY=-17.873 EndZ=0
  constraints (14):
    c: Coincident(g0,g-1)
    c: PointOnObject(g0,g-3)
    c: PointOnObject(g0,g-3)
    c: Coincident(g1,g0)
    c: PointOnObject(g1,g-3)
    c: PointOnObject(g1,g-3)
    c: Coincident(g2,g1)
    c: Coincident(g2,g1)
    c: Horizontal(g2)
    c: PointOnObject(g-4,g2)
    c: Coincident(g3,g0)
    c: Coincident(g3,g0)
    c: Horizontal(g3)
    c: PointOnObject(g-5,g3)
FEATURE [PartDesign::Pad] Pad012
  BaseFeature = -> Pad011
  Direction = (1,1,1)
  Length = 2
  Length2 = 100
  Profile = -> Sketch018
  Type = 0
FEATURE [Sketcher::SketchObject] Sketch019
  ExternalGeometry = -> [Pad012]
  FullyConstrained = true
  MapMode = 5
  Placement = pos=(0,0,-20) rot=(1,0,0;3.14159rad)
  Support = -> [Pad012]
  sketch-geometry (3):
    g0: Circle CenterX=-18 CenterY=4 CenterZ=0 NormalX=0 NormalY=0 NormalZ=1 AngleXU=0 Radius=1.5
    g1: Circle CenterX=-18 CenterY=-4 CenterZ=0 NormalX=0 NormalY=0 NormalZ=1 AngleXU=0 Radius=1.5
    g2: Circle CenterX=0 CenterY=0 CenterZ=0 NormalX=0 NormalY=0 NormalZ=1 AngleXU=0 Radius=23.9
  constraints (7):
    c: Radius(g1) = 1.5
    c: Equal(g1,g0)
    c: Symmetric(g0,g1,g-1)
    c: DistanceX(g0) = -18
    c: DistanceY(g0) = 4
    c: Radius(g2) = 23.9
    c: Coincident(g2,g-1)
FEATURE [PartDesign::Pad] Pad013
  BaseFeature = -> Pad012
  Direction = (1,1,1)
  Length = 2
  Length2 = 100
  Profile = -> Sketch019
  Type = 0
FEATURE [PartDesign::Chamfer] Chamfer004
  Angle = 45
  Base = -> Pad013 [Edge42]
  BaseFeature = -> Pad013
  ChamferType = 0
  FlipDirection = false
  Size = 1
  Size2 = 1
  SupportTransform = false
FEATURE [PartDesign::Body] Body011  label="couvercle_coiffe_V1"
  Group = -> [Sketch016,Pad010,Chamfer003,Sketch017,Pad011,Sketch018,Pad012,Sketch019,Pad013,Chamfer004]
  Origin = -> Origin011
  Placement = pos=(0,0,260.3) rot=(0,0,1;0rad)
  Tip = -> Chamfer004
FEATURE [Mesh::Feature] Mesh001  label="couvercle_coiffe_V1 (Meshed)"
FEATURE [Sketcher::SketchObject] Sketch020
  FullyConstrained = true
  MapMode = 5
  Support = -> [XY_Plane012]
  sketch-geometry (2):
    g0: Circle CenterX=0 CenterY=0 CenterZ=0 NormalX=0 NormalY=0 NormalZ=1 AngleXU=0 Radius=9.25
    g1: Circle CenterX=0 CenterY=0 CenterZ=0 NormalX=0 NormalY=0 NormalZ=1 AngleXU=0 Radius=11.75
  constraints (4):
    c: Coincident(g0,g-1)
    c: Coincident(g1,g0)
    c: Radius(g1) = 11.75
    c: Radius(g0) = 9.25
FEATURE [PartDesign::Pad] Pad014
  Direction = (1,1,1)
  Length = 70
  Length2 = 100
  Profile = -> Sketch020
  Type = 0
FEATURE [Sketcher::SketchObject] Sketch021
  FullyConstrained = true
  MapMode = 5
  Placement = pos=(0,0,0) rot=(1,0,0;3.14159rad)
  Support = -> [Pad014]
  sketch-geometry (4):
    g0: LineSegment StartX=-15.74 StartY=1.5 StartZ=0 EndX=15.74 EndY=1.5 EndZ=0
    g1: LineSegment StartX=15.74 StartY=1.5 StartZ=0 EndX=15.74 EndY=-1.5 EndZ=0
    g2: LineSegment StartX=15.74 StartY=-1.5 StartZ=0 EndX=-15.74 EndY=-1.5 EndZ=0
    g3: LineSegment StartX=-15.74 StartY=-1.5 StartZ=0 EndX=-15.74 EndY=1.5 EndZ=0
  constraints (11):
    c: Coincident(g0,g1)
    c: Coincident(g1,g2)
    c: Coincident(g2,g3)
    c: Coincident(g3,g0)
    c: Horizontal(g0)
    c: Horizontal(g2)
    c: Vertical(g1)
    c: Vertical(g3)
    c: Symmetric(g1,g0,g-1)
    c: DistanceX(g2,g2) = 31.48
    c: DistanceY(g1,g1) = 3
FEATURE [PartDesign::Pocket] Pocket004
  BaseFeature = -> Pad014
  Length = 67
  Length2 = 100
  Profile = -> Sketch021
  Type = 0
FEATURE [PartDesign::Chamfer] Chamfer005
  Angle = 45
  Base = -> Pocket004 [Edge3,Edge7]
  BaseFeature = -> Pocket004
  ChamferType = 0
  FlipDirection = false
  Size = 2
  Size2 = 1
  SupportTransform = false
FEATURE [Sketcher::SketchObject] Sketch022
  FullyConstrained = true
  MapMode = 5
  Placement = pos=(0,0,0) rot=(1,0,0;3.14159rad)
  Support = -> [Chamfer005]
  sketch-geometry (4):
    g0: LineSegment StartX=-1.5 StartY=15.795 StartZ=0 EndX=1.5 EndY=15.795 EndZ=0
    g1: LineSegment StartX=1.5 StartY=15.795 StartZ=0 EndX=1.5 EndY=-15.795 EndZ=0
    g2: LineSegment StartX=1.5 StartY=-15.795 StartZ=0 EndX=-1.5 EndY=-15.795 EndZ=0
    g3: LineSegment StartX=-1.5 StartY=-15.795 StartZ=0 EndX=-1.5 EndY=15.795 EndZ=0
  constraints (11):
    c: Coincident(g0,g1)
    c: Coincident(g1,g2)
    c: Coincident(g2,g3)
    c: Coincident(g3,g0)
    c: Horizontal(g0)
    c: Horizontal(g2)
    c: Vertical(g1)
    c: Vertical(g3)
    c: Symmetric(g1,g0,g-1)
    c: DistanceX(g2,g2) = 3
    c: DistanceY(g1,g1) = 31.59
FEATURE [PartDesign::Pocket] Pocket005
  BaseFeature = -> Chamfer005
  Length = 67
  Length2 = 100
  Profile = -> Sketch022
  Type = 0
FEATURE [PartDesign::Body] Body012  label="Adaptateur_moteur_V1"
  Group = -> [Sketch020,Pad014,Sketch021,Pocket004,Chamfer005,Sketch022,Pocket005]
  Origin = -> Origin012
  Placement = pos=(0,8e-15,69) rot=(1,0,0;3.14159rad)
  Tip = -> Pocket005
FEATURE [Mesh::Feature] Mesh002  label="couvercle_coiffe_V1 (Meshed)001"
FEATURE [Sketcher::SketchObject] Sketch023
  FullyConstrained = true
  MapMode = 5
  Support = -> [XY_Plane013]
  sketch-geometry (2):
    g0: Circle CenterX=0 CenterY=0 CenterZ=0 NormalX=0 NormalY=0 NormalZ=1 AngleXU=0 Radius=9.25
    g1: Circle CenterX=0 CenterY=0 CenterZ=0 NormalX=0 NormalY=0 NormalZ=1 AngleXU=0 Radius=11.75
  constraints (4):
    c: Coincident(g0,g-1)
    c: Coincident(g1,g0)
    c: Radius(g1) = 11.75
    c: Radius(g0) = 9.25
FEATURE [PartDesign::Pad] Pad015
  Direction = (1,1,1)
  Length = 70
  Length2 = 100
  Profile = -> Sketch023
  Type = 0
FEATURE [Sketcher::SketchObject] Sketch025
  FullyConstrained = true
  MapMode = 5
  Placement = pos=(0,0,0) rot=(1,0,0;3.14159rad)
  Support = -> [Pad015]
  sketch-geometry (4):
    g0: LineSegment StartX=-15.74 StartY=1.5 StartZ=0 EndX=15.74 EndY=1.5 EndZ=0
    g1: LineSegment StartX=15.74 StartY=1.5 StartZ=0 EndX=15.74 EndY=-1.5 EndZ=0
    g2: LineSegment StartX=15.74 StartY=-1.5 StartZ=0 EndX=-15.74 EndY=-1.5 EndZ=0
    g3: LineSegment StartX=-15.74 StartY=-1.5 StartZ=0 EndX=-15.74 EndY=1.5 EndZ=0
  constraints (11):
    c: Coincident(g0,g1)
    c: Coincident(g1,g2)
    c: Coincident(g2,g3)
    c: Coincident(g3,g0)
    c: Horizontal(g0)
    c: Horizontal(g2)
    c: Vertical(g1)
    c: Vertical(g3)
    c: Symmetric(g1,g0,g-1)
    c: DistanceX(g2,g2) = 31.48
    c: DistanceY(g1,g1) = 3
FEATURE [PartDesign::Pocket] Pocket007
  BaseFeature = -> Pad015
  Length = 67
  Length2 = 100
  Profile = -> Sketch025
  Type = 0
FEATURE [PartDesign::Chamfer] Chamfer006
  Angle = 45
  Base = -> Pocket007 [Edge3,Edge7]
  BaseFeature = -> Pocket007
  ChamferType = 0
  FlipDirection = false
  Size = 2
  Size2 = 1
  SupportTransform = false
FEATURE [Sketcher::SketchObject] Sketch024
  ExternalGeometry = -> [Chamfer006]
  FullyConstrained = true
  MapMode = 5
  Placement = pos=(0,0,0) rot=(1,0,0;3.14159rad)
  Support = -> [Chamfer006]
  sketch-geometry (8):
    g0: LineSegment StartX=-1.5 StartY=13.94 StartZ=0 EndX=11.6539 EndY=13.94 EndZ=0
    g1: LineSegment StartX=11.6539 StartY=13.94 StartZ=0 EndX=11.6539 EndY=1.5 EndZ=0
    g2: LineSegment StartX=11.6539 StartY=1.5 StartZ=0 EndX=-1.5 EndY=1.5 EndZ=0
    g3: LineSegment StartX=-1.5 StartY=1.5 StartZ=0 EndX=-1.5 EndY=13.94 EndZ=0
    g4: LineSegment StartX=-11.6539 StartY=-1.5 StartZ=0 EndX=1.5 EndY=-1.5 EndZ=0
    g5: LineSegment StartX=1.5 StartY=-1.5 StartZ=0 EndX=1.5 EndY=-13.94 EndZ=0
    g6: LineSegment StartX=1.5 StartY=-13.94 StartZ=0 EndX=-11.6539 EndY=-13.94 EndZ=0
    g7: LineSegment StartX=-11.6539 StartY=-13.94 StartZ=0 EndX=-11.6539 EndY=-1.5 EndZ=0
  constraints (21):
    c: Coincident(g0,g1)
    c: Coincident(g1,g2)
    c: Coincident(g2,g3)
    c: Coincident(g3,g0)
    c: Horizontal(g0)
    c: Horizontal(g2)
    c: Vertical(g1)
    c: Vertical(g3)
    c: Coincident(g1,g-3)
    c: DistanceX(g-2,g0) = -1.5
    c: DistanceY(g1,g1) = 12.44
    c: Coincident(g4,g5)
    c: Coincident(g5,g6)
    c: Coincident(g6,g7)
    c: Coincident(g7,g4)
    c: Horizontal(g4)
    c: Horizontal(g6)
    c: Vertical(g5)
    c: Vertical(g7)
    c: Coincident(g4,g-4)
    c: Symmetric(g5,g0,g-1)
FEATURE [PartDesign::Pocket] Pocket006
  BaseFeature = -> Chamfer006
  Length = 67
  Length2 = 100
  Profile = -> Sketch024
  Type = 0
FEATURE [PartDesign::Body] Body013  label="Adaptateur_moteur_V2"
  Group = -> [Sketch023,Pad015,Sketch025,Pocket007,Chamfer006,Sketch024,Pocket006]
  Origin = -> Origin013
  Placement = pos=(0,8e-15,-141) rot=(1,0,0;3.14159rad)
  Tip = -> Pocket006
FEATURE [TechDraw::DrawViewPart] View  label="Coiffe"
  CoarseView = false
  Direction = (0,-1,0)
  Focus = 100
  HardHidden = false
  IsoCount = 0
  IsoHidden = false
  IsoVisible = false
  LockPosition = false
  Perspective = false
  Rotation = 0
  Scale = 0.5
  ScaleType = 0
  SeamHidden = false
  SeamVisible = true
  SmoothHidden = false
  SmoothVisible = true
  Source = -> [Body010]
  X = 141.396
  XDirection = (1,0,0)
  Y = 132.536
FEATURE [TechDraw::DrawViewSection] SectionView  label="Section  - 1"
  BaseView = -> View
  CoarseView = false
  CutSurfaceDisplay = 2
  Direction = (1,0,0)
  FileGeomPattern = <path>
  FileHatchPattern = <path>
  Focus = 100
  FuseBeforeCut = false
  HardHidden = false
  HatchScale = 1
  IsoCount = 0
  IsoHidden = false
  IsoVisible = false
  LockPosition = false
  NameGeomPattern = Diamond
  Perspective = false
  Rotation = 0
  ScaleType = 0
  SeamHidden = false
  SeamVisible = true
  SectionDirection = 1
  SectionNormal = (1,0,0)
  SectionOrigin = (0,0,358.13)
  SmoothHidden = false
  SmoothVisible = true
  Source = -> [Body010]
  X = 71.6286
  XDirection = (0,1,0)
  Y = 114.948
FEATURE [TechDraw::DrawViewSection] SectionView001  label="Section  - 2"
  BaseView = -> View
  CoarseView = false
  CutSurfaceDisplay = 2
  Direction = (0,0,-1)
  FileGeomPattern = <path>
  FileHatchPattern = <path>
  Focus = 100
  FuseBeforeCut = false
  HardHidden = false
  HatchScale = 1
  IsoCount = 0
  IsoHidden = false
  IsoVisible = false
  LockPosition = false
  NameGeomPattern = Diamond
  Perspective = false
  Rotation = 0
  ScaleType = 0
  SeamHidden = false
  SeamVisible = true
  SectionDirection = 2
  SectionNormal = (0,0,-1)
  SectionOrigin = (0,0,358.13)
  SmoothHidden = false
  SmoothVisible = true
  Source = -> [Body010]
  X = 217.697
  XDirection = (1,0,0)
  Y = 161.361
FEATURE [TechDraw::DrawViewSection] SectionView002  label="Section  - 3"
  BaseView = -> View
  CoarseView = false
  CutSurfaceDisplay = 2
  Direction = (0,0,-1)
  FileGeomPattern = <path>
  FileHatchPattern = <path>
  Focus = 100
  FuseBeforeCut = false
  HardHidden = false
  HatchScale = 1
  IsoCount = 0
  IsoHidden = false
  IsoVisible = false
  LockPosition = false
  NameGeomPattern = Diamond
  Perspective = false
  Rotation = 0
  ScaleType = 0
  SeamHidden = false
  SeamVisible = true
  SectionDirection = 2
  SectionNormal = (0,0,-1)
  SectionOrigin = (0,0,294.13)
  SmoothHidden = false
  SmoothVisible = true
  Source = -> [Body010]
  X = 218.545
  XDirection = (1,0,0)
  Y = 99.0481
FEATURE [TechDraw::DrawViewDimension] Dimension
  Arbitrary = false
  ArbitraryTolerances = false
  EqualTolerance = true
  FormatSpec = ⌀%.2f
  FormatSpecOverTolerance = %+.2f
  FormatSpecUnderTolerance = %+.2f
  Inverted = false
  LockPosition = false
  MeasureType = 1
  OverTolerance = 0
  References2D = -> [SectionView001]
  Rotation = 0
  ScaleType = 0
  TheoreticalExact = false
  Type = 5
  UnderTolerance = 0
  X = 0
  Y = 0
FEATURE [TechDraw::DrawViewDimension] Dimension001
  Arbitrary = false
  ArbitraryTolerances = false
  EqualTolerance = true
  FormatSpec = ⌀%.2f
  FormatSpecOverTolerance = %+.2f
  FormatSpecUnderTolerance = %+.2f
  Inverted = false
  LockPosition = false
  MeasureType = 1
  OverTolerance = 0
  References2D = -> [SectionView002]
  Rotation = 0
  ScaleType = 0
  TheoreticalExact = false
  Type = 5
  UnderTolerance = 0
  X = 0
  Y = 0
FEATURE [TechDraw::DrawPage] Page
  KeepUpdated = true
  NextBalloonIndex = 1
  ProjectionType = 0
  Template = -> Template
  Views = -> [View,SectionView,SectionView001,SectionView002,Dimension,Dimension001]
note: 6 file-system paths scrubbed to <path> (originals preserved in the JSON sidecar)
